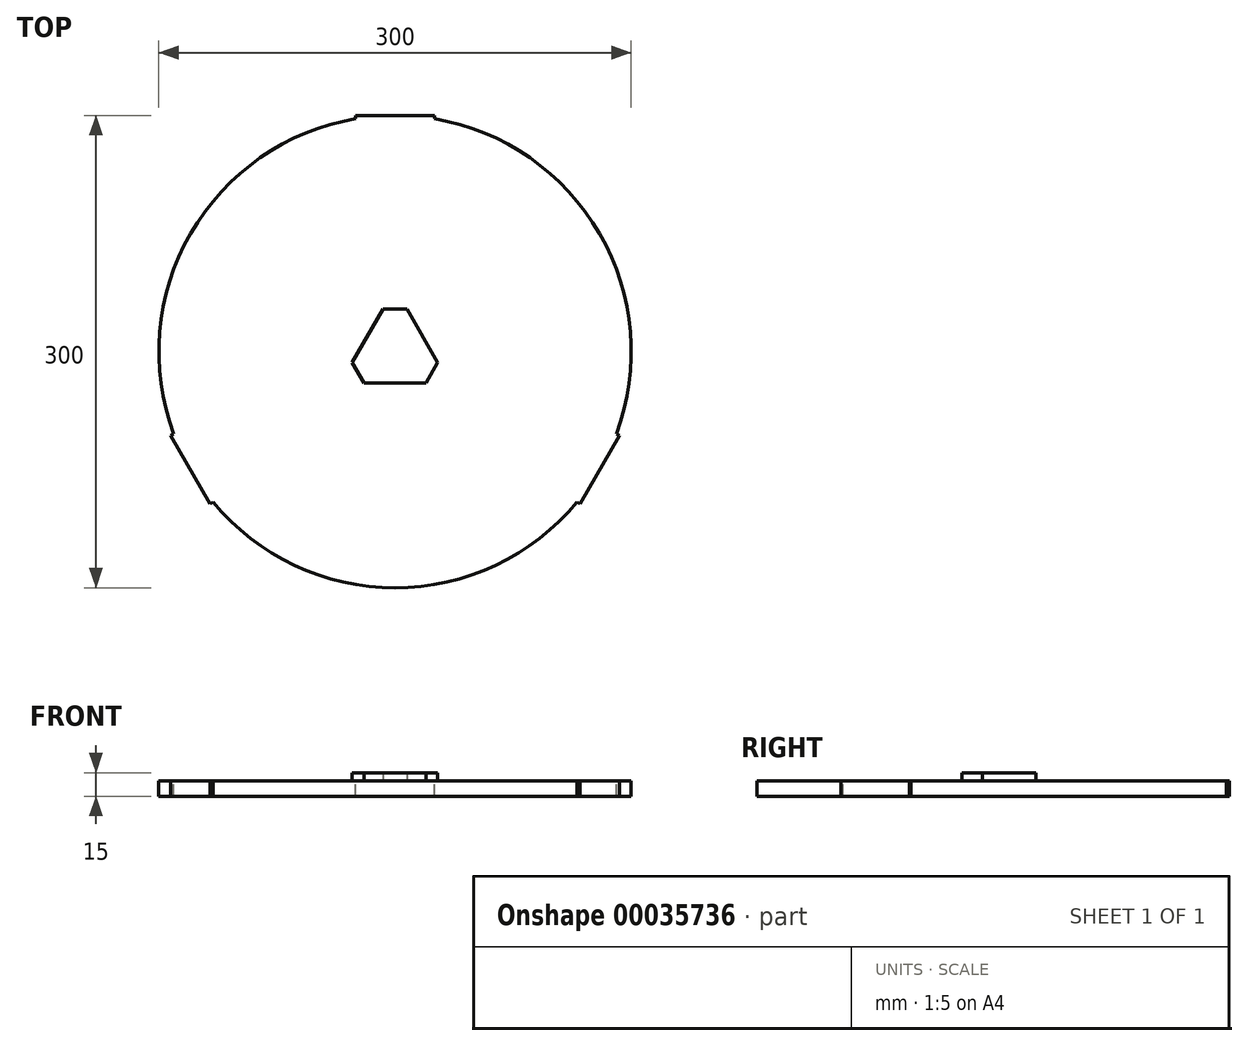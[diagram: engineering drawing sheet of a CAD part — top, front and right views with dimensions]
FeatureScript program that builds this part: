
annotation { "Feature Type Name" : "Feature", "Feature Type Description" : "" }
export const myFeature = defineFeature(function(context is Context, id is Id, definition is map)
    precondition{}
    {
        {
            var Q0;
            Q0=qCreatedBy(makeId("Top.planeOp"),FACE);
            var sketch = newSketch(context, id + "F0", { "sketchPlane" : qUnion([Q0])});
            skArc(sketch, "E0", {"start": v(-115.59, -95.6) * mm, "mid": v(0, -150) * mm, "end": v(115.59, -95.6) * mm});
            skLineSegment(sketch, "E1", {"start": v(0, 0) * mm, "end": v(0, 200.82) * mm, "construction": true});
            skPoint(sketch, "E2", {"position": v(0, 150) * mm});
            skPoint(sketch, "E3.1.0", {"position": v(-129.9, -75) * mm});
            skPoint(sketch, "E3.2.0", {"position": v(129.9, -75) * mm});
            skLineSegment(sketch, "E4", {"start": v(-129.9, -75) * mm, "end": v(-142.4, -53.35) * mm});
            skLineSegment(sketch, "E5", {"start": v(-129.9, -75) * mm, "end": v(-117.4, -96.65) * mm});
            skLineSegment(sketch, "E6", {"start": v(-142.4, -53.35) * mm, "end": v(-140.59, -52.3) * mm});
            skLineSegment(sketch, "E7", {"start": v(-117.4, -96.65) * mm, "end": v(-115.59, -95.6) * mm});
            skPoint(sketch, "E8", {"position": v(-140.59, -52.3) * mm});
            skLineSegment(sketch, "E9.1.0", {"start": v(129.9, -75) * mm, "end": v(142.4, -53.35) * mm});
            skLineSegment(sketch, "E9.1.1", {"start": v(129.9, -75) * mm, "end": v(117.4, -96.65) * mm});
            skLineSegment(sketch, "E9.1.2", {"start": v(117.4, -96.65) * mm, "end": v(115.59, -95.6) * mm});
            skLineSegment(sketch, "E9.1.3", {"start": v(142.4, -53.35) * mm, "end": v(140.59, -52.3) * mm});
            skLineSegment(sketch, "E9.2.0", {"start": v(0, 150) * mm, "end": v(-25, 150) * mm});
            skLineSegment(sketch, "E9.2.1", {"start": v(0, 150) * mm, "end": v(25, 150) * mm});
            skLineSegment(sketch, "E9.2.2", {"start": v(25, 150) * mm, "end": v(25, 147.9) * mm});
            skLineSegment(sketch, "E9.2.3", {"start": v(-25, 150) * mm, "end": v(-25, 147.9) * mm});
            skArc(sketch, "E10.trimOffspring", {"start": v(140.59, -52.3) * mm, "mid": v(129.9, 75) * mm, "end": v(25, 147.9) * mm});
            skArc(sketch, "E11.trimOffspring", {"start": v(-25, 147.9) * mm, "mid": v(-129.9, 75) * mm, "end": v(-140.59, -52.3) * mm});
            skSolve(sketch);
        }
        {
            var Q0;
            Q0 = qSketchRegion(id + "F0", true);
            extrude(context, id + "F1", {"entities" : qUnion([Q0]), "oppositeDirection" : true, "depth" : 10 * mm});
        }
        {
            var Q0;
            Q0=qCreatedBy(makeId("Top.planeOp"),FACE);
            var sketch = newSketch(context, id + "F2", { "sketchPlane" : qUnion([Q0])});
            skCircle(sketch, "E12.cCircle", {"center": v(0, 0) * mm, "radius": 40 * mm, "construction": true});
            skLineSegment(sketch, "E12.0", {"start": v(7.5, 27) * mm, "end": v(27.14, -7) * mm});
            skLineSegment(sketch, "E12.1", {"start": v(19.64, -20) * mm, "end": v(-19.64, -20) * mm});
            skLineSegment(sketch, "E12.2", {"start": v(-27.14, -7) * mm, "end": v(-7.5, 27) * mm});
            skCircle(sketch, "E13.cCircle", {"center": v(0, 0) * mm, "radius": 54.02 * mm, "construction": true});
            skLineSegment(sketch, "E13.0", {"start": v(0, -54.02) * mm, "end": v(-8.64, -39.06) * mm});
            skLineSegment(sketch, "E13.1", {"start": v(-46.78, 27) * mm, "end": v(-29.5, 27) * mm});
            skLineSegment(sketch, "E13.2", {"start": v(46.78, 27) * mm, "end": v(38.14, 12.05) * mm});
            skPoint(sketch, "E14", {"position": v(27.14, -7) * mm});
            skPoint(sketch, "E15", {"position": v(19.64, -20) * mm});
            skPoint(sketch, "E16.orphan", {"position": v(0, 40) * mm});
            skLineSegment(sketch, "E17.trimOffspring", {"start": v(-7.5, 27) * mm, "end": v(7.5, 27) * mm});
            skLineSegment(sketch, "E18.trimOffspring", {"start": v(-38.14, 12.05) * mm, "end": v(-46.78, 27) * mm});
            skPoint(sketch, "E19.orphan", {"position": v(-34.64, -20) * mm});
            skLineSegment(sketch, "E20.trimOffspring", {"start": v(-19.64, -20) * mm, "end": v(-27.14, -7) * mm});
            skLineSegment(sketch, "E21.trimOffspring", {"start": v(8.64, -39.06) * mm, "end": v(0, -54.02) * mm});
            skLineSegment(sketch, "E22.trimOffspring", {"start": v(27.14, -7) * mm, "end": v(19.64, -20) * mm});
            skLineSegment(sketch, "E23.trimOffspring", {"start": v(29.5, 27) * mm, "end": v(46.78, 27) * mm});
            skPoint(sketch, "E24.orphan", {"position": v(34.64, -20) * mm});
            skSolve(sketch);
        }
        {
            var Q0;
            Q0=makeQuery(id+"F2.imprint","IMPRINT",FACE,{"disambiguationData":[TD([[makeQuery(id+"F2.imprint","IMPRINT",EDGE,{"derivedFrom":sQuery(id+"F2.wireOp",EDGE,"E12.0")}),-1.0]])]});
            extrude(context, id + "F3", {"entities" : qUnion([Q0]), "depth" : 5 * mm});
        }
    });
